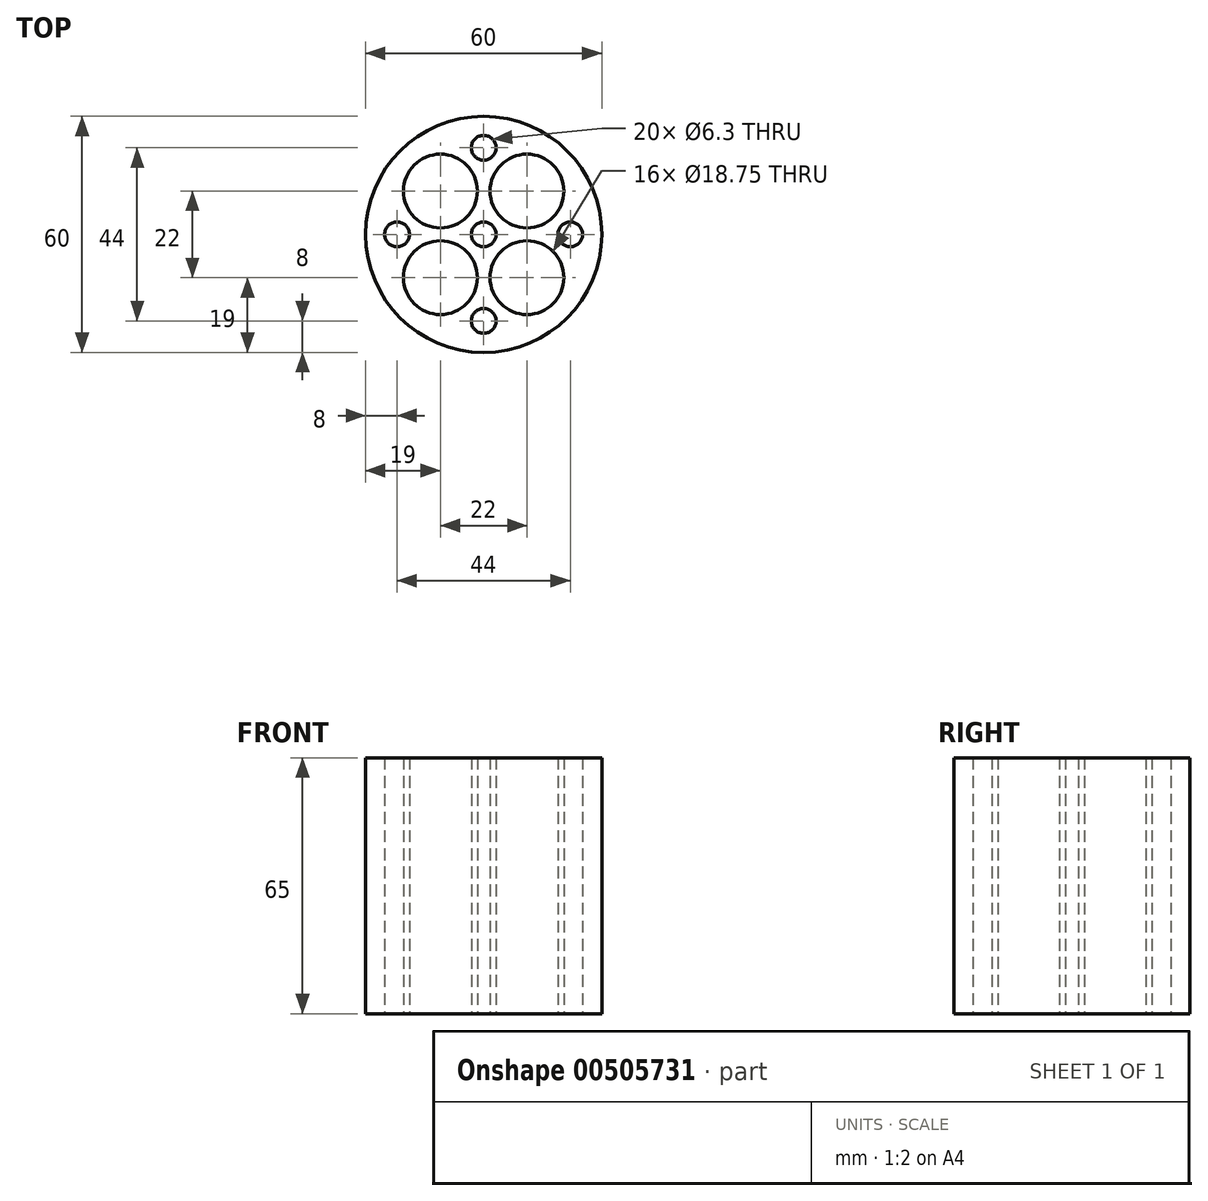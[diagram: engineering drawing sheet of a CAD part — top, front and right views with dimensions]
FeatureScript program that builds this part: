
annotation { "Feature Type Name" : "Feature", "Feature Type Description" : "" }
export const myFeature = defineFeature(function(context is Context, id is Id, definition is map)
    precondition{}
    {
        {
            var Q0;
            Q0=qCreatedBy(makeId("Top.planeOp"),FACE);
            var sketch = newSketch(context, id + "F0", { "sketchPlane" : qUnion([Q0])});
            skCircle(sketch, "E0", {"center": v(0, 0) * mm, "radius": 30 * mm});
            skLineSegment(sketch, "E1.bottom", {"start": v(-11, 11) * mm, "end": v(11, 11) * mm, "construction": true});
            skLineSegment(sketch, "E1.top", {"start": v(-11, -11) * mm, "end": v(11, -11) * mm, "construction": true});
            skLineSegment(sketch, "E1.left", {"start": v(-11, 11) * mm, "end": v(-11, -11) * mm, "construction": true});
            skLineSegment(sketch, "E1.right", {"start": v(11, 11) * mm, "end": v(11, -11) * mm, "construction": true});
            skCircle(sketch, "E2", {"center": v(-11, 11) * mm, "radius": 9.38 * mm});
            skCircle(sketch, "E3", {"center": v(11, 11) * mm, "radius": 9.38 * mm});
            skCircle(sketch, "E4", {"center": v(11, -11) * mm, "radius": 9.38 * mm});
            skCircle(sketch, "E5", {"center": v(-11, -11) * mm, "radius": 9.38 * mm});
            skCircle(sketch, "E6", {"center": v(-22, 0) * mm, "radius": 3.15 * mm});
            skCircle(sketch, "E7", {"center": v(0, 0) * mm, "radius": 3.15 * mm});
            skCircle(sketch, "E8", {"center": v(22, 0) * mm, "radius": 3.15 * mm});
            skCircle(sketch, "E9", {"center": v(0, 22) * mm, "radius": 3.15 * mm});
            skCircle(sketch, "E10", {"center": v(0, -22) * mm, "radius": 3.15 * mm});
            skSolve(sketch);
        }
        {
            var Q0;
            Q0=makeQuery(id+"F0.imprint","IMPRINT",FACE,{"disambiguationData":[TD([[makeQuery(id+"F0.imprint","IMPRINT",EDGE,{"derivedFrom":sQuery(id+"F0.wireOp",EDGE,"E0")}),1.0]])]});
            extrude(context, id + "F1", {"entities" : qUnion([Q0]), "depth" : 65 * mm});
        }
    });
